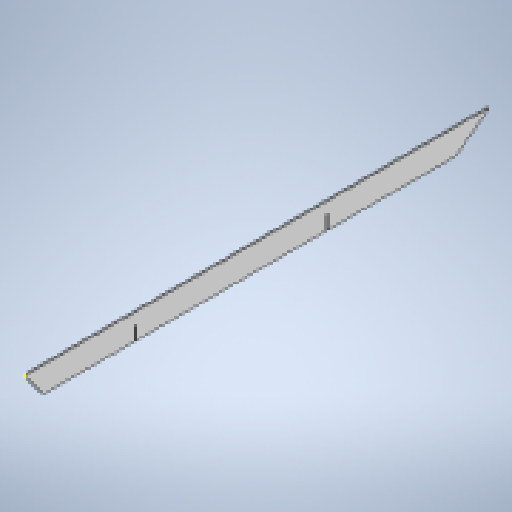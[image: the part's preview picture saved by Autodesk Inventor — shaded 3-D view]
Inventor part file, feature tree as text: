
AUTODESK INVENTOR PART (.ipt)
format: ipt  version: 2025 (Build 290162010, 162A)  size: 288,256 bytes
history: native  units: mm
features: other x4, sketch x3, sheet_metal_op x1, chamfer x1, extrude x1
ambient origin geometry x8: Origin, YZ Plane, XZ Plane, XY Plane, X Axis, Y Axis, Z Axis, Center Point
bodies: Body1 (feature_tree)
feature tree (10):
  sheet_metal_op  "Face1"
  other  "Corner Chamfer1"
  chamfer  "Corner Round1"
  extrude  "Extrusion1"  Depth=920.0mm
  other  "Mark1"
  sketch  "Sketch2"  dims[d3=380.0mm d6=380.0mm d7=380.0mm d28=920.0mm]
  other  "Plate2"
  sketch  "Sketch3"  dims[d29=50.0mm]
  sketch  "Sketch4"  dims[d30=3.0mm d31=6.335545mm d32=9.372418mm d33=3.0mm d34=6.0mm d35=45.0deg d36=9.372418mm d37=6.0mm d38=219.04mm d39=26.0mm d40=3.0mm d41=219.04mm d42=599.04mm d43=3.0mm d44=26.0mm d45=0.0mm d46=0.0mm]
  other  "Definition1"
